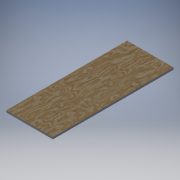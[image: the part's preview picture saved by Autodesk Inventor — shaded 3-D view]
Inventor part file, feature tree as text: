
AUTODESK INVENTOR PART (.ipt)
format: ipt  version: 2018.2 (Build 222227000, 227)  size: 108,544 bytes
history: native  units: in
note: dims shown in document units (in); Inventor stores cm internally (conversion verified against a paired STEP export)
features: extrude x1, sketch x1
ambient origin geometry x8: Origin, YZ Plane, XZ Plane, XY Plane, X Axis, Y Axis, Z Axis, Center Point
bodies: Solid1 (feature_tree)
feature tree (2):
  extrude  "Extrusion1"  Depth=45.381in
  sketch  "Sketch1"  dims[d0=17.459in d1=45.381in d2=0.75in d3=0.0in]
